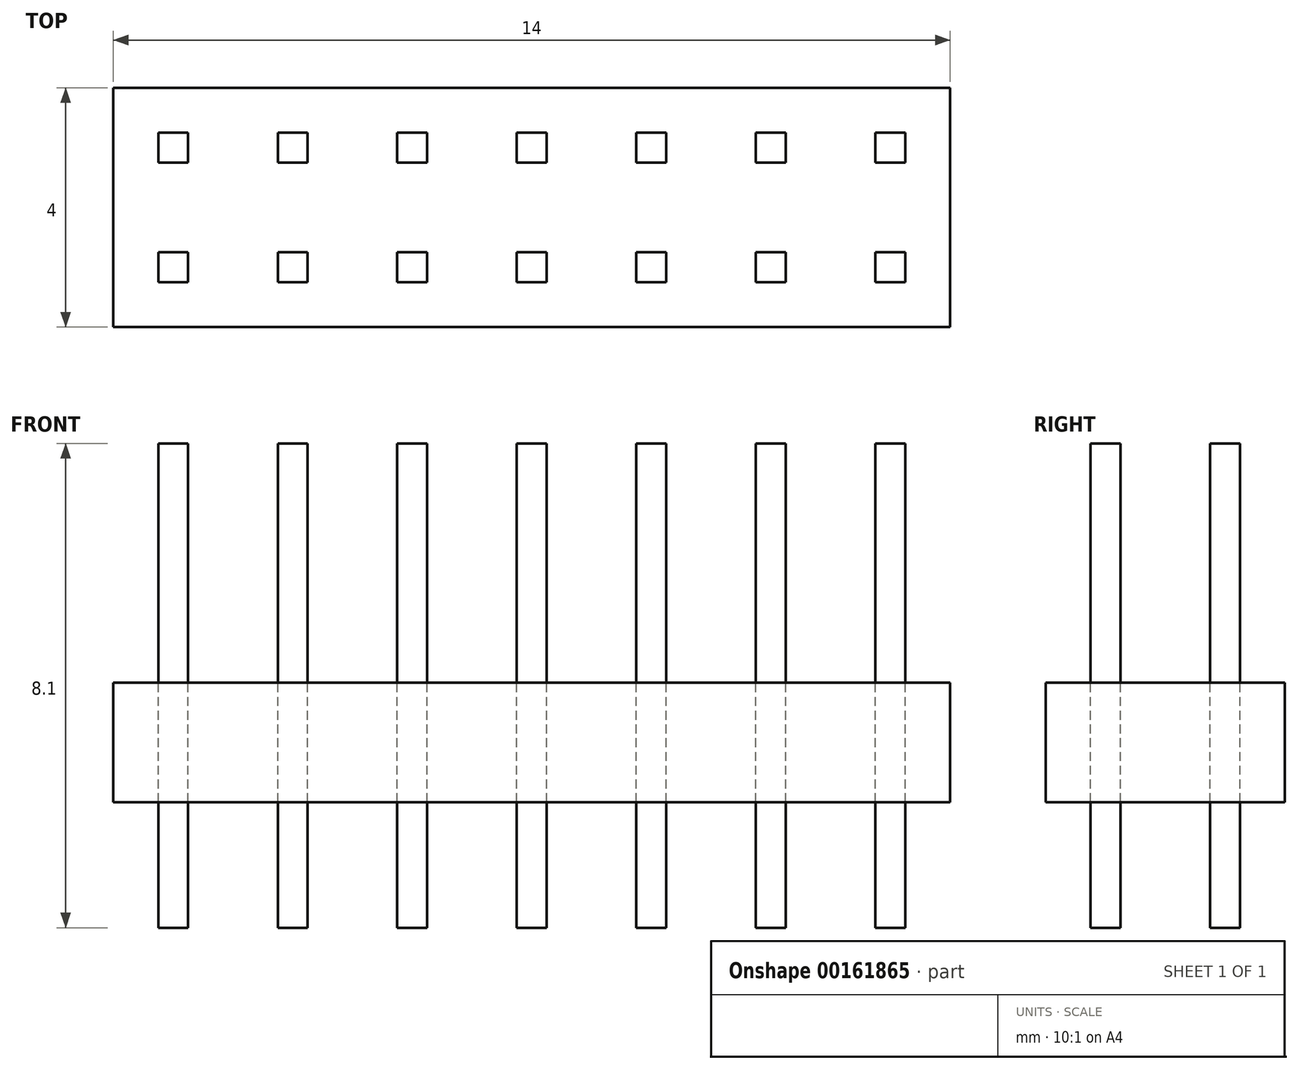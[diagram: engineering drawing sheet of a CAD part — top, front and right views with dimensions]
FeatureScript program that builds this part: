
annotation { "Feature Type Name" : "Feature", "Feature Type Description" : "" }
export const myFeature = defineFeature(function(context is Context, id is Id, definition is map)
    precondition{}
    {
        {
            var Q0;
            Q0=qCreatedBy(makeId("Top.planeOp"),FACE);
            var sketch = newSketch(context, id + "F0", { "sketchPlane" : qUnion([Q0])});
            skLineSegment(sketch, "E0.bottom", {"start": v(-9, 2) * mm, "end": v(9, 2) * mm});
            skLineSegment(sketch, "E0.top", {"start": v(-9, -2) * mm, "end": v(9, -2) * mm});
            skLineSegment(sketch, "E0.left", {"start": v(-9, 2) * mm, "end": v(-9, -2) * mm});
            skLineSegment(sketch, "E0.right", {"start": v(9, 2) * mm, "end": v(9, -2) * mm});
            skSolve(sketch);
        }
        {
            var Q0;
            Q0=qSketchRegion(id+"F0",true);
            extrude(context, id + "F1", {"entities" : qUnion([Q0]), "depth" : 2 * mm});
        }
        {
            var Q0;
            Q0=makeQuery(id+"F1.opExtrude","CAP_FACE",FACE,{"disambiguationData":[OSD([sQuery(id+"F0.wireOp",EDGE,"E0.bottom"),sQuery(id+"F0.wireOp",EDGE,"E0.top"),sQuery(id+"F0.wireOp",EDGE,"E0.left"),sQuery(id+"F0.wireOp",EDGE,"E0.right")])],"isStart":false});
            var sketch = newSketch(context, id + "F2", { "sketchPlane" : qUnion([Q0])});
            skLineSegment(sketch, "E1.bottom", {"start": v(-0.25, 1.25) * mm, "end": v(0.25, 1.25) * mm});
            skLineSegment(sketch, "E1.top", {"start": v(-0.25, 0.75) * mm, "end": v(0.25, 0.75) * mm});
            skLineSegment(sketch, "E1.left", {"start": v(-0.25, 1.25) * mm, "end": v(-0.25, 0.75) * mm});
            skLineSegment(sketch, "E1.right", {"start": v(0.25, 1.25) * mm, "end": v(0.25, 0.75) * mm});
            skLineSegment(sketch, "E2.MirrorCS", {"start": v(-0.25, -1.25) * mm, "end": v(0.25, -1.25) * mm});
            skLineSegment(sketch, "E3.MirrorCS", {"start": v(-0.25, -0.75) * mm, "end": v(0.25, -0.75) * mm});
            skLineSegment(sketch, "E4.MirrorCS", {"start": v(-0.25, -1.25) * mm, "end": v(-0.25, -0.75) * mm});
            skLineSegment(sketch, "E5.MirrorCS", {"start": v(0.25, -1.25) * mm, "end": v(0.25, -0.75) * mm});
            skLineSegment(sketch, "E6.MirrorCS", {"start": v(-1.75, -1.25) * mm, "end": v(-1.75, -0.75) * mm});
            skLineSegment(sketch, "E7.MirrorCS", {"start": v(-1.75, -0.75) * mm, "end": v(-2.25, -0.75) * mm});
            skLineSegment(sketch, "E8.MirrorCS", {"start": v(-2.25, -1.25) * mm, "end": v(-2.25, -0.75) * mm});
            skLineSegment(sketch, "E9.MirrorCS", {"start": v(-1.75, -1.25) * mm, "end": v(-2.25, -1.25) * mm});
            skLineSegment(sketch, "E10.MirrorCS", {"start": v(-2.25, 1.25) * mm, "end": v(-2.25, 0.75) * mm});
            skLineSegment(sketch, "E11.MirrorCS", {"start": v(-1.75, 1.25) * mm, "end": v(-1.75, 0.75) * mm});
            skLineSegment(sketch, "E12.MirrorCS", {"start": v(-1.75, 1.25) * mm, "end": v(-2.25, 1.25) * mm});
            skLineSegment(sketch, "E13.MirrorCS", {"start": v(-1.75, 0.75) * mm, "end": v(-2.25, 0.75) * mm});
            skLineSegment(sketch, "E14.MirrorCS", {"start": v(-4.25, -1.25) * mm, "end": v(-4.25, -0.75) * mm});
            skLineSegment(sketch, "E15.MirrorCS", {"start": v(-4.25, -0.75) * mm, "end": v(-3.75, -0.75) * mm});
            skLineSegment(sketch, "E16.MirrorCS", {"start": v(-4.25, 0.75) * mm, "end": v(-3.75, 0.75) * mm});
            skLineSegment(sketch, "E17.MirrorCS", {"start": v(-4.25, 1.25) * mm, "end": v(-4.25, 0.75) * mm});
            skLineSegment(sketch, "E18.MirrorCS", {"start": v(-4.25, 1.25) * mm, "end": v(-3.75, 1.25) * mm});
            skLineSegment(sketch, "E19.MirrorCS", {"start": v(-3.75, 1.25) * mm, "end": v(-3.75, 0.75) * mm});
            skLineSegment(sketch, "E20.MirrorCS", {"start": v(-4.25, -1.25) * mm, "end": v(-3.75, -1.25) * mm});
            skLineSegment(sketch, "E21.MirrorCS", {"start": v(-3.75, -1.25) * mm, "end": v(-3.75, -0.75) * mm});
            skLineSegment(sketch, "E22.MirrorCS", {"start": v(-5.75, -1.25) * mm, "end": v(-6.25, -1.25) * mm});
            skLineSegment(sketch, "E23.MirrorCS", {"start": v(-5.75, 0.75) * mm, "end": v(-6.25, 0.75) * mm});
            skLineSegment(sketch, "E24.MirrorCS", {"start": v(-5.75, -0.75) * mm, "end": v(-6.25, -0.75) * mm});
            skLineSegment(sketch, "E25.MirrorCS", {"start": v(-5.75, 1.25) * mm, "end": v(-6.25, 1.25) * mm});
            skLineSegment(sketch, "E26.MirrorCS", {"start": v(-6.25, 1.25) * mm, "end": v(-6.25, 0.75) * mm});
            skLineSegment(sketch, "E27.MirrorCS", {"start": v(-5.75, -1.25) * mm, "end": v(-5.75, -0.75) * mm});
            skLineSegment(sketch, "E28.MirrorCS", {"start": v(-6.25, -1.25) * mm, "end": v(-6.25, -0.75) * mm});
            skLineSegment(sketch, "E29.MirrorCS", {"start": v(-5.75, 1.25) * mm, "end": v(-5.75, 0.75) * mm});
            skLineSegment(sketch, "E30.MirrorCS", {"start": v(-8.25, 0.75) * mm, "end": v(-7.75, 0.75) * mm});
            skLineSegment(sketch, "E31.MirrorCS", {"start": v(-7.75, 1.25) * mm, "end": v(-7.75, 0.75) * mm});
            skLineSegment(sketch, "E32.MirrorCS", {"start": v(-8.25, 1.25) * mm, "end": v(-8.25, 0.75) * mm});
            skLineSegment(sketch, "E33.MirrorCS", {"start": v(-7.75, -1.25) * mm, "end": v(-7.75, -0.75) * mm});
            skLineSegment(sketch, "E34.MirrorCS", {"start": v(-8.25, 1.25) * mm, "end": v(-7.75, 1.25) * mm});
            skLineSegment(sketch, "E35.MirrorCS", {"start": v(-8.25, -1.25) * mm, "end": v(-8.25, -0.75) * mm});
            skLineSegment(sketch, "E36.MirrorCS", {"start": v(-8.25, -1.25) * mm, "end": v(-7.75, -1.25) * mm});
            skLineSegment(sketch, "E37.MirrorCS", {"start": v(-8.25, -0.75) * mm, "end": v(-7.75, -0.75) * mm});
            skLineSegment(sketch, "E38.MirrorCS", {"start": v(8.25, 1.25) * mm, "end": v(7.75, 1.25) * mm});
            skLineSegment(sketch, "E39.MirrorCS", {"start": v(5.75, -1.25) * mm, "end": v(5.75, -0.75) * mm});
            skLineSegment(sketch, "E40.MirrorCS", {"start": v(4.25, 1.25) * mm, "end": v(3.75, 1.25) * mm});
            skLineSegment(sketch, "E41.MirrorCS", {"start": v(8.25, 0.75) * mm, "end": v(7.75, 0.75) * mm});
            skLineSegment(sketch, "E42.MirrorCS", {"start": v(4.25, -1.25) * mm, "end": v(4.25, -0.75) * mm});
            skLineSegment(sketch, "E43.MirrorCS", {"start": v(5.75, 1.25) * mm, "end": v(6.25, 1.25) * mm});
            skLineSegment(sketch, "E44.MirrorCS", {"start": v(6.25, 1.25) * mm, "end": v(6.25, 0.75) * mm});
            skLineSegment(sketch, "E45.MirrorCS", {"start": v(5.75, -1.25) * mm, "end": v(6.25, -1.25) * mm});
            skLineSegment(sketch, "E46.MirrorCS", {"start": v(8.25, -1.25) * mm, "end": v(8.25, -0.75) * mm});
            skLineSegment(sketch, "E47.MirrorCS", {"start": v(6.25, -1.25) * mm, "end": v(6.25, -0.75) * mm});
            skLineSegment(sketch, "E48.MirrorCS", {"start": v(7.75, 1.25) * mm, "end": v(7.75, 0.75) * mm});
            skLineSegment(sketch, "E49.MirrorCS", {"start": v(3.75, 1.25) * mm, "end": v(3.75, 0.75) * mm});
            skLineSegment(sketch, "E50.MirrorCS", {"start": v(4.25, -0.75) * mm, "end": v(3.75, -0.75) * mm});
            skLineSegment(sketch, "E51.MirrorCS", {"start": v(4.25, 1.25) * mm, "end": v(4.25, 0.75) * mm});
            skLineSegment(sketch, "E52.MirrorCS", {"start": v(7.75, -1.25) * mm, "end": v(7.75, -0.75) * mm});
            skLineSegment(sketch, "E53.MirrorCS", {"start": v(5.75, -0.75) * mm, "end": v(6.25, -0.75) * mm});
            skLineSegment(sketch, "E54.MirrorCS", {"start": v(1.75, 0.75) * mm, "end": v(2.25, 0.75) * mm});
            skLineSegment(sketch, "E55.MirrorCS", {"start": v(8.25, -0.75) * mm, "end": v(7.75, -0.75) * mm});
            skLineSegment(sketch, "E56.MirrorCS", {"start": v(1.75, 1.25) * mm, "end": v(2.25, 1.25) * mm});
            skLineSegment(sketch, "E57.MirrorCS", {"start": v(4.25, 0.75) * mm, "end": v(3.75, 0.75) * mm});
            skLineSegment(sketch, "E58.MirrorCS", {"start": v(8.25, 1.25) * mm, "end": v(8.25, 0.75) * mm});
            skLineSegment(sketch, "E59.MirrorCS", {"start": v(1.75, -1.25) * mm, "end": v(1.75, -0.75) * mm});
            skLineSegment(sketch, "E60.MirrorCS", {"start": v(3.75, -1.25) * mm, "end": v(3.75, -0.75) * mm});
            skLineSegment(sketch, "E61.MirrorCS", {"start": v(1.75, -0.75) * mm, "end": v(2.25, -0.75) * mm});
            skLineSegment(sketch, "E62.MirrorCS", {"start": v(2.25, -1.25) * mm, "end": v(2.25, -0.75) * mm});
            skLineSegment(sketch, "E63.MirrorCS", {"start": v(1.75, 1.25) * mm, "end": v(1.75, 0.75) * mm});
            skLineSegment(sketch, "E64.MirrorCS", {"start": v(2.25, 1.25) * mm, "end": v(2.25, 0.75) * mm});
            skLineSegment(sketch, "E65.MirrorCS", {"start": v(4.25, -1.25) * mm, "end": v(3.75, -1.25) * mm});
            skLineSegment(sketch, "E66.MirrorCS", {"start": v(8.25, -1.25) * mm, "end": v(7.75, -1.25) * mm});
            skLineSegment(sketch, "E67.MirrorCS", {"start": v(5.75, 0.75) * mm, "end": v(6.25, 0.75) * mm});
            skLineSegment(sketch, "E68.MirrorCS", {"start": v(1.75, -1.25) * mm, "end": v(2.25, -1.25) * mm});
            skLineSegment(sketch, "E69.MirrorCS", {"start": v(5.75, 1.25) * mm, "end": v(5.75, 0.75) * mm});
            skSolve(sketch);
        }
        {
            var Q0;
            Q0=qSketchRegion(id+"F2",true);
            extrude(context, id + "F3", {"entities" : qUnion([Q0]), "depth" : 4 * mm});
        }
        {
            var Q0;
            Q0=qSketchRegion(id+"F2",true);
            extrude(context, id + "F4", {"entities" : qUnion([Q0]), "oppositeDirection" : true, "depth" : 4.1 * mm});
        }
        {
            var Q0;
            Q0=makeQuery(id+"F1.opExtrude","SWEPT_FACE",FACE,{"disambiguationData":[OSD([sQuery(id+"F0.wireOp",EDGE,"E0.top")])]});
            var sketch = newSketch(context, id + "F5", { "sketchPlane" : qUnion([Q0])});
            skLineSegment(sketch, "E70.bottom", {"start": v(7, 6.32) * mm, "end": v(11.36, 6.32) * mm});
            skLineSegment(sketch, "E70.top", {"start": v(7, -4.96) * mm, "end": v(11.36, -4.96) * mm});
            skLineSegment(sketch, "E70.left", {"start": v(7, 6.32) * mm, "end": v(7, -4.96) * mm});
            skLineSegment(sketch, "E70.right", {"start": v(11.36, 6.32) * mm, "end": v(11.36, -4.96) * mm});
            skLineSegment(sketch, "E71.MirrorCS", {"start": v(-11.36, 6.32) * mm, "end": v(-11.36, -4.96) * mm});
            skLineSegment(sketch, "E72.MirrorCS", {"start": v(-7, 6.32) * mm, "end": v(-7, -4.96) * mm});
            skLineSegment(sketch, "E73.MirrorCS", {"start": v(-7, 6.32) * mm, "end": v(-11.36, 6.32) * mm});
            skLineSegment(sketch, "E74.MirrorCS", {"start": v(-7, -4.96) * mm, "end": v(-11.36, -4.96) * mm});
            skSolve(sketch);
        }
        {
            var Q0;
            Q0 = qSketchRegion(id + "F5", true);
            extrude(context, id + "F6", {"entities" : qUnion([Q0]), "operationType" : NewBodyOperationType.REMOVE, "endBound" : BoundingType.THROUGH_ALL, "oppositeDirection" : true, "depth" : 25 * mm});
        }
    });
